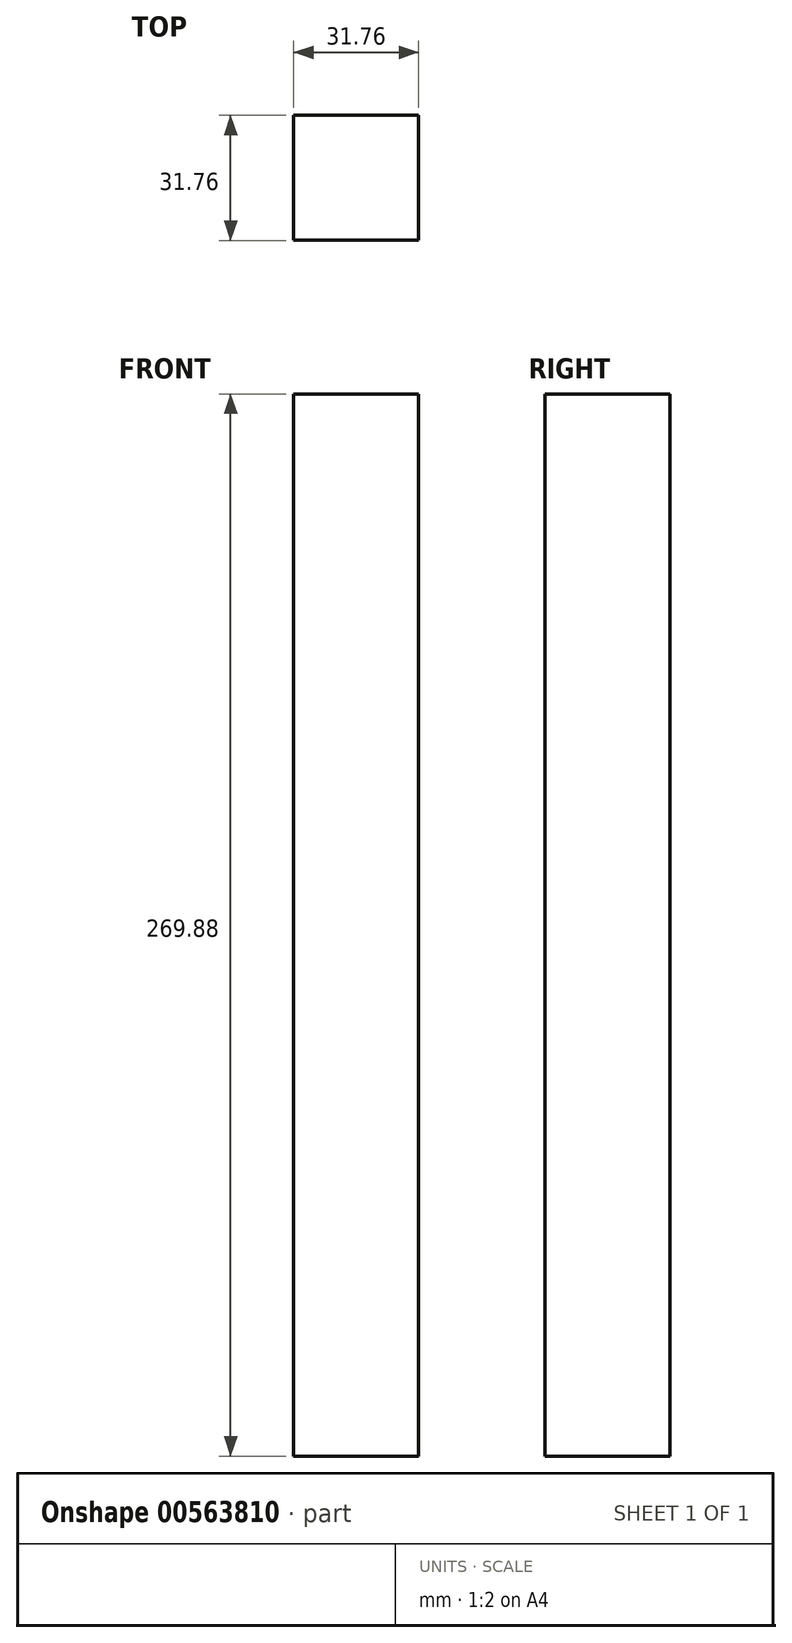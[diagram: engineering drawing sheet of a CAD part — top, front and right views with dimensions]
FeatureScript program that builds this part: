
annotation { "Feature Type Name" : "Feature", "Feature Type Description" : "" }
export const myFeature = defineFeature(function(context is Context, id is Id, definition is map)
    precondition{}
    {
        {
            var Q0;
            Q0=qCreatedBy(makeId("Top.planeOp"),FACE);
            var sketch = newSketch(context, id + "F0", { "sketchPlane" : qUnion([Q0])});
            skLineSegment(sketch, "E0.bottom", {"start": v(-15.87, 15.88) * mm, "end": v(15.88, 15.88) * mm});
            skLineSegment(sketch, "E0.top", {"start": v(-15.88, -15.88) * mm, "end": v(15.87, -15.88) * mm});
            skLineSegment(sketch, "E0.left", {"start": v(-15.87, 15.88) * mm, "end": v(-15.88, -15.88) * mm});
            skLineSegment(sketch, "E0.right", {"start": v(15.88, 15.88) * mm, "end": v(15.87, -15.88) * mm});
            skPoint(sketch, "E0.middle", {"position": v(0, 0) * mm});
            skSolve(sketch);
        }
        {
            var Q0;
            Q0=makeQuery(id+"F0.imprint","IMPRINT",FACE,{"disambiguationData":[TD([[makeQuery(id+"F0.imprint","IMPRINT",EDGE,{"derivedFrom":sQuery(id+"F0.wireOp",EDGE,"E0.bottom")}),-1.0]])]});
            extrude(context, id + "F1", {"entities" : qUnion([Q0]), "endBound" : BoundingType.SYMMETRIC, "depth" : 269.88 * mm, "offsetDistance" : 25.4 * mm});
        }
    });
